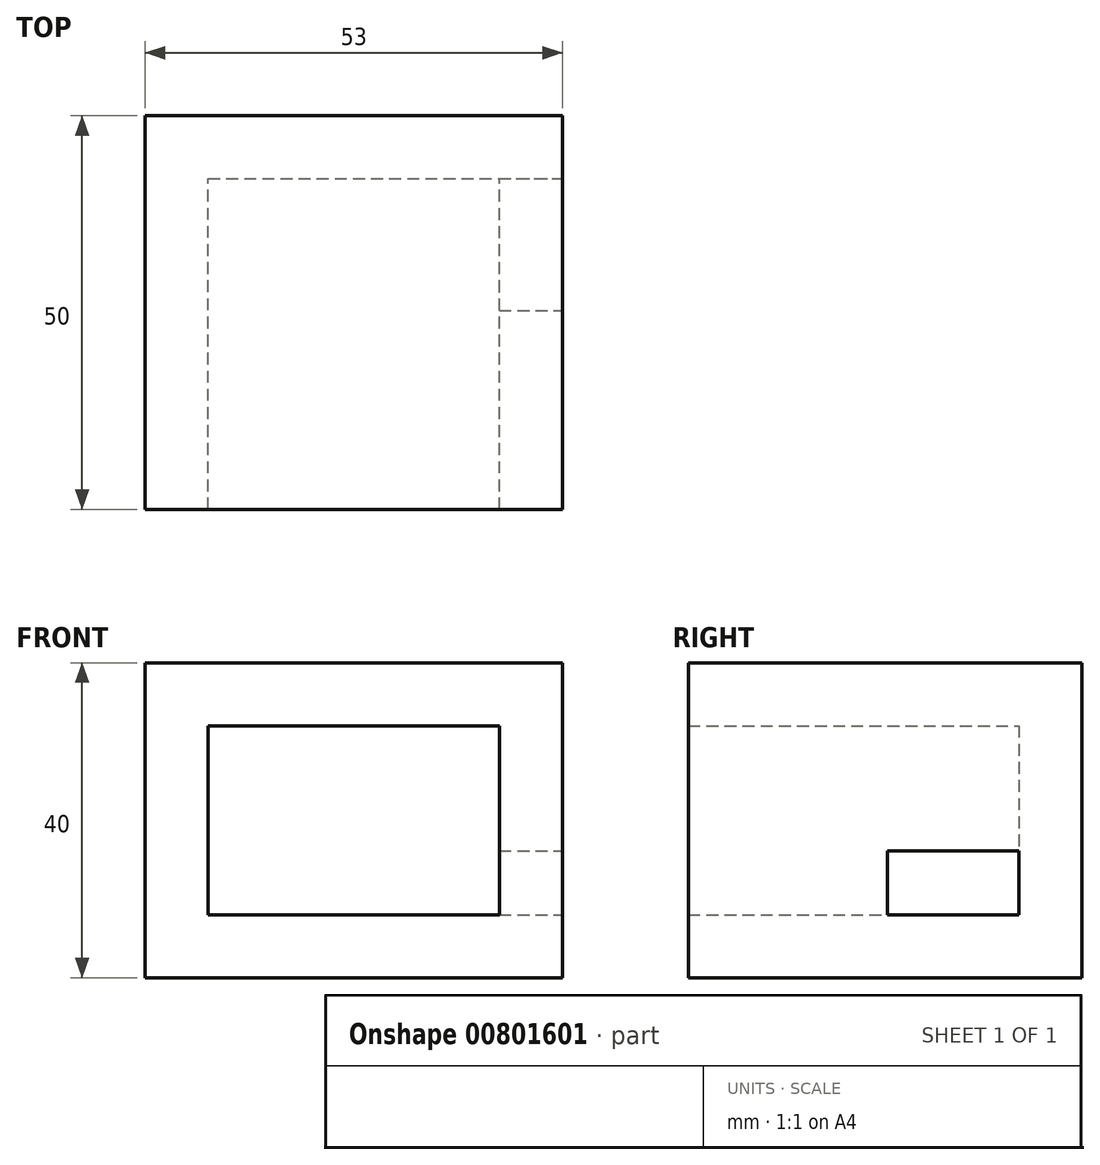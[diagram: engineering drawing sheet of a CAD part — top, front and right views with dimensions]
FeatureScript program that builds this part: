
annotation { "Feature Type Name" : "Feature", "Feature Type Description" : "" }
export const myFeature = defineFeature(function(context is Context, id is Id, definition is map)
    precondition{}
    {
        {
            var Q0;
            Q0=qCreatedBy(makeId("Front.planeOp"),FACE);
            var sketch = newSketch(context, id + "F0", { "sketchPlane" : qUnion([Q0])});
            skLineSegment(sketch, "E0.bottom", {"start": v(-13.48, 23.9) * mm, "end": v(39.52, 23.9) * mm});
            skLineSegment(sketch, "E0.top", {"start": v(-13.48, -16.1) * mm, "end": v(39.52, -16.1) * mm});
            skLineSegment(sketch, "E0.left", {"start": v(-13.48, 23.9) * mm, "end": v(-13.48, -16.1) * mm});
            skLineSegment(sketch, "E0.right", {"start": v(39.52, 23.9) * mm, "end": v(39.52, -16.1) * mm});
            skSolve(sketch);
        }
        {
            var Q0;
            Q0=makeQuery(id+"F0.imprint","IMPRINT",FACE,{"disambiguationData":[TD([[makeQuery(id+"F0.imprint","IMPRINT",EDGE,{"derivedFrom":sQuery(id+"F0.wireOp",EDGE,"E0.bottom")}),-1.0]])]});
            extrude(context, id + "F1", {"entities" : qUnion([Q0]), "depth" : 50 * mm, "offsetDistance" : 25 * mm});
        }
        {
            var Q0;
            Q0=makeQuery(id+"F1.opExtrude","CAP_FACE",FACE,{"disambiguationData":[OSD([sQuery(id+"F0.wireOp",EDGE,"E0.bottom"),sQuery(id+"F0.wireOp",EDGE,"E0.top"),sQuery(id+"F0.wireOp",EDGE,"E0.left"),sQuery(id+"F0.wireOp",EDGE,"E0.right")])],"isStart":false});
            var Q1;
            Q1=makeQuery(id+"F1.opExtrude","SWEPT_BODY",BODY,{"disambiguationData":[OSD([sQuery(id+"F0.wireOp",EDGE,"E0.bottom"),sQuery(id+"F0.wireOp",EDGE,"E0.top"),sQuery(id+"F0.wireOp",EDGE,"E0.left"),sQuery(id+"F0.wireOp",EDGE,"E0.right")])]});
            shell(context, id + "F2", {"entities" : qUnion([Q0]), "parts" : qUnion([Q1]), "thickness" : 8 * mm});
        }
        {
            var Q0;
            Q0=makeQuery(id+"F1.opExtrude","SWEPT_FACE",FACE,{"disambiguationData":[OSD([sQuery(id+"F0.wireOp",EDGE,"E0.right")])]});
            var sketch = newSketch(context, id + "F3", { "sketchPlane" : qUnion([Q0])});
            skLineSegment(sketch, "E1.bottom", {"start": v(-24.73, 0) * mm, "end": v(-8, 0) * mm});
            skLineSegment(sketch, "E1.top", {"start": v(-24.73, -8.1) * mm, "end": v(-8, -8.1) * mm});
            skLineSegment(sketch, "E1.left", {"start": v(-24.73, 0) * mm, "end": v(-24.73, -8.1) * mm});
            skLineSegment(sketch, "E1.right", {"start": v(-8, 0) * mm, "end": v(-8, -8.1) * mm});
            skSolve(sketch);
        }
        {
            var Q0;
            Q0=makeQuery(id+"F3.imprint","IMPRINT",FACE,{"disambiguationData":[TD([[makeQuery(id+"F3.imprint","IMPRINT",EDGE,{"derivedFrom":sQuery(id+"F3.wireOp",EDGE,"E1.bottom")}),-1.0]])]});
            extrude(context, id + "F4", {"entities" : qUnion([Q0]), "operationType" : NewBodyOperationType.REMOVE, "depth" : -8 * mm, "offsetDistance" : 25 * mm});
        }
    });
